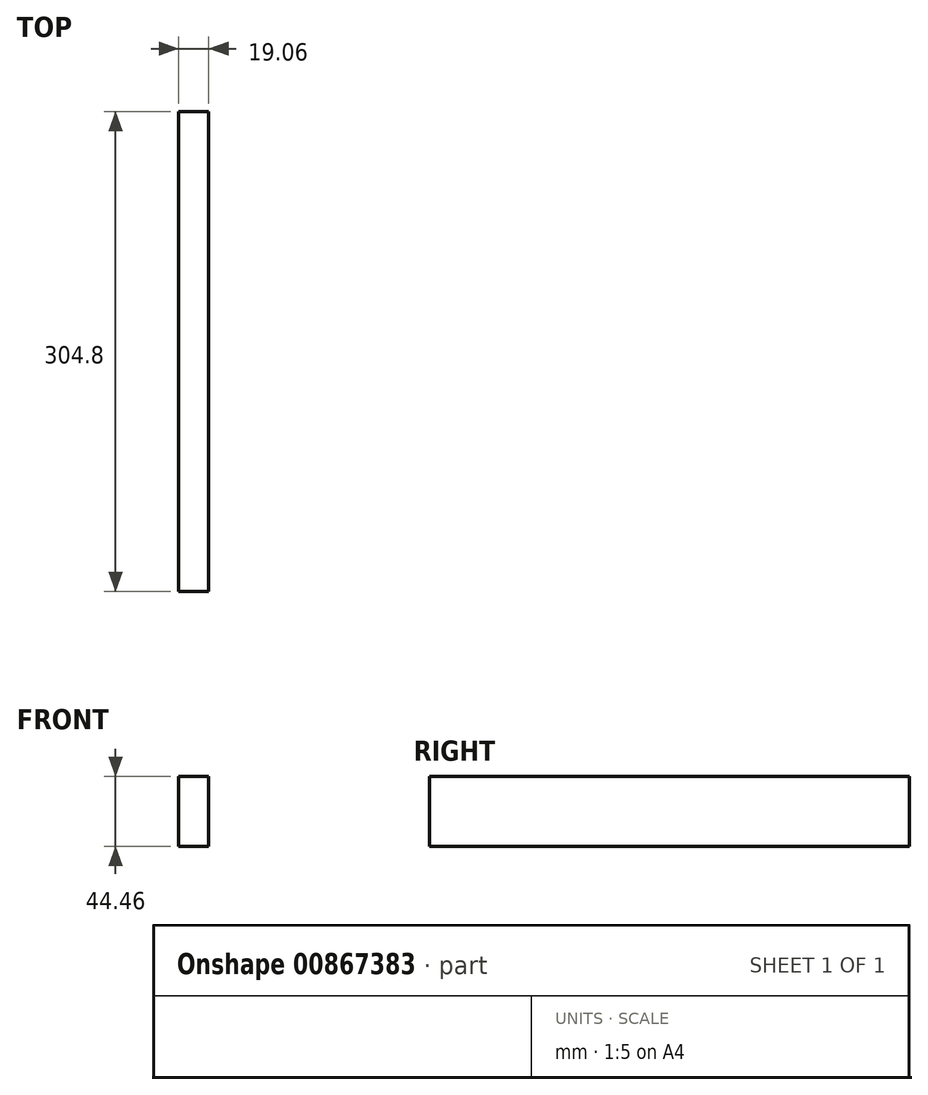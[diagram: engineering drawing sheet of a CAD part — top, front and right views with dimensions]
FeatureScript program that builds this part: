
annotation { "Feature Type Name" : "Feature", "Feature Type Description" : "" }
export const myFeature = defineFeature(function(context is Context, id is Id, definition is map)
    precondition{}
    {
        {
            var Q0;
            Q0=qCreatedBy(makeId("Front.planeOp"),FACE);
            var sketch = newSketch(context, id + "F0", { "sketchPlane" : qUnion([Q0])});
            skLineSegment(sketch, "E0.bottom", {"start": v(9.53, -22.23) * mm, "end": v(-9.53, -22.23) * mm});
            skLineSegment(sketch, "E0.top", {"start": v(9.53, 22.23) * mm, "end": v(-9.52, 22.23) * mm});
            skLineSegment(sketch, "E0.left", {"start": v(9.53, -22.22) * mm, "end": v(9.53, 22.23) * mm});
            skLineSegment(sketch, "E0.right", {"start": v(-9.53, -22.23) * mm, "end": v(-9.52, 22.23) * mm});
            skPoint(sketch, "E0.middle", {"position": v(0, 0) * mm});
            skSolve(sketch);
        }
        {
            var Q0;
            Q0=makeQuery(id+"F0.imprint","IMPRINT",FACE,{"disambiguationData":[TD([[makeQuery(id+"F0.imprint","IMPRINT",EDGE,{"derivedFrom":sQuery(id+"F0.wireOp",EDGE,"E0.bottom")}),-1.0]])]});
            extrude(context, id + "F1", {"entities" : qUnion([Q0]), "depth" : 304.8 * mm, "offsetDistance" : 25.4 * mm});
        }
    });
